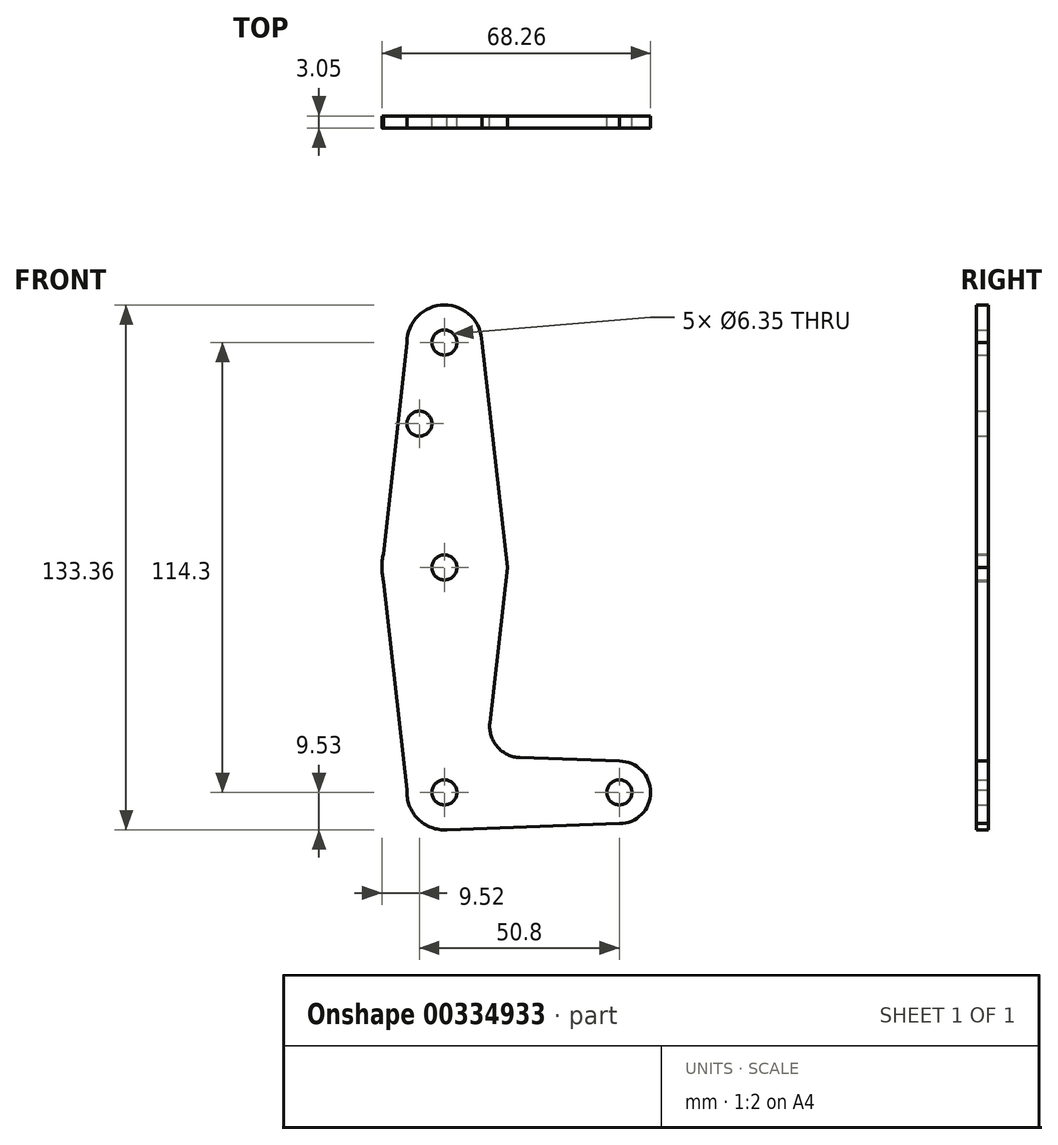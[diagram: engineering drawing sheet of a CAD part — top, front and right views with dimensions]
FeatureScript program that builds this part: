
annotation { "Feature Type Name" : "Feature", "Feature Type Description" : "" }
export const myFeature = defineFeature(function(context is Context, id is Id, definition is map)
    precondition{}
    {
        {
            var Q0;
            Q0=qCreatedBy(makeId("Front.planeOp"),FACE);
            var sketch = newSketch(context, id + "F0", { "sketchPlane" : qUnion([Q0])});
            skCircle(sketch, "E0", {"center": v(0, 114.3) * mm, "radius": 9.53 * mm});
            skCircle(sketch, "E1", {"center": v(0, 57.15) * mm, "radius": 15.88 * mm});
            skCircle(sketch, "E2", {"center": v(0, 0) * mm, "radius": 9.53 * mm});
            skCircle(sketch, "E3", {"center": v(44.45, 0) * mm, "radius": 7.94 * mm});
            skLineSegment(sketch, "E4", {"start": v(0, 114.3) * mm, "end": v(0, 0) * mm, "construction": true});
            skLineSegment(sketch, "E5", {"start": v(0, 0) * mm, "end": v(44.45, 0) * mm, "construction": true});
            skLineSegment(sketch, "E6", {"start": v(9.53, 114.3) * mm, "end": v(15.98, 57.15) * mm});
            skLineSegment(sketch, "E7", {"start": v(15.98, 57.15) * mm, "end": v(11.56, 17.67) * mm});
            skLineSegment(sketch, "E8", {"start": v(-9.52, 114.3) * mm, "end": v(-15.88, 57.15) * mm});
            skLineSegment(sketch, "E9", {"start": v(-15.88, 57.15) * mm, "end": v(-9.42, 0) * mm});
            skLineSegment(sketch, "E10", {"start": v(0, -9.53) * mm, "end": v(44.45, -7.94) * mm});
            skLineSegment(sketch, "E11", {"start": v(44.45, 7.94) * mm, "end": v(19.18, 8.84) * mm});
            skCircle(sketch, "E12", {"center": v(0, 114.3) * mm, "radius": 3.18 * mm});
            skCircle(sketch, "E13", {"center": v(0, 57.15) * mm, "radius": 3.18 * mm});
            skCircle(sketch, "E14", {"center": v(0, 0) * mm, "radius": 3.18 * mm});
            skCircle(sketch, "E15", {"center": v(44.45, 0) * mm, "radius": 3.18 * mm});
            skCircle(sketch, "E16", {"center": v(-6.35, 93.68) * mm, "radius": 3.18 * mm});
            skPoint(sketch, "E17.newPointA", {"position": v(9.58, 0) * mm});
            skPoint(sketch, "E17.newPointB", {"position": v(0, 9.53) * mm});
            skArc(sketch, "E17.filletArc", {"start": v(11.56, 17.67) * mm, "mid": v(13.44, 11.6) * mm, "end": v(19.18, 8.84) * mm});
            skSolve(sketch);
        }
        {
            var Q0;
            Q0 = qSketchRegion(id + "F0", true);
            extrude(context, id + "F1", {"entities" : qUnion([Q0]), "depth" : 3.05 * mm});
        }
    });
